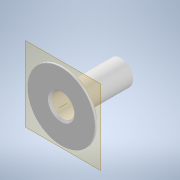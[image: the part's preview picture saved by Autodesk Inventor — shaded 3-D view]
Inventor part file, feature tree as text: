
AUTODESK INVENTOR PART (.ipt)
format: ipt  version: 2021 (Build 250183000, 183)  size: 159,744 bytes
history: native  units: mm
features: other x5, extrude x4, sketch x4, chamfer x3, reference x3
ambient origin geometry x8: Origin, YZ Plane, XZ Plane, XY Plane, X Axis, Y Axis, Z Axis, Center Point
bodies: Body1 (feature_tree)
feature tree (19):
  other  "Bryła1"
  other  "Oś konstrukcyjna1"
  other  "Płaszczyzna konstrukcyjna1"
  extrude  "Wyciągnięcie proste1"  Depth=145.0mm
  extrude  "Wyciągnięcie proste2"  Depth=60.0mm
  extrude  "Wyciągnięcie proste3"  Depth=5.0mm TaperAngle=0.0deg
  chamfer  "Faza1"  Distance=65.0mm
  chamfer  "Faza2"  Distance=150.0mm
  extrude  "Wyciągnięcie proste4"  Depth=3.0mm TaperAngle=0.0deg
  chamfer  "Faza3"  Distance=1.0mm Angle=45.0deg
  sketch  "Szkic1"
  reference  "Odniesienie1"
  reference  "Odniesienie2"
  sketch  "Szkic2"
  sketch  "Szkic3"
  sketch  "Szkic4"
  reference  "Odniesienie3"
  other  "Zespół1"
  other  "garnek:1"
